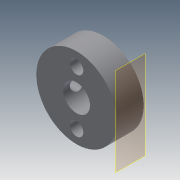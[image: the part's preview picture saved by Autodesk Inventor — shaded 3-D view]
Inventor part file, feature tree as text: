
AUTODESK INVENTOR PART (.ipt)
format: ipt  version: 2015 (Build 190159000, 159)  size: 109,056 bytes
history: native  units: mm
features: extrude x3, sketch x3, plane x1, projected_geometry x1
ambient origin geometry x8: Origin, YZ Plane, XZ Plane, XY Plane, X Axis, Y Axis, Z Axis, Center Point
bodies: Solid1 (feature_tree)
feature tree (8):
  extrude  "Extrusion1"  Depth=10.0mm
  plane  "Work Plane1"
  extrude  "Extrusion2"  Depth=15.0mm
  extrude  "Extrusion3"  Depth=5.0mm
  sketch  "Sketch1"  dims[d0=30.0mm d1=10.0mm]
  sketch  "Sketch2"  dims[d2=10.0mm d3=0.0mm d4=15.0mm]
  sketch  "Sketch3"  dims[d5=5.0mm d6=5.0mm d7=10.0mm d8=0.0mm d10=5.0mm d11=10.0mm d12=10.0mm d13=0.0mm]
  projected_geometry  "Projected Loop1"
